# Revit family: Add_On_Board-Teknion-CQCAB_Routes-R2022
name_source: partatom
category: Furniture
units: mm (PartAtom-declared; Revit-internal decimal feet)

## family parameters
Always vertical = Yes
Cut with Voids When Loaded = No
OmniClass Number = 23.40.20.00
OmniClass Title = General Furniture and Specialties
Render Appearance Source = Family Geometry
Room Calculation Point = No
Shared = Yes
Work Plane-Based = No

## types (3) — shared parameters
2D Add On Board = Yes
Assembly Code = E2020200
Manufacturer = Teknion
Manufacturer Fax = 416.661.4586
Part Number = CQCAB
Product Documentation Link = https://assets.teknion.com
Product Line = Routes
Product Page URL = https://www.teknion.com
Series = Routes
Sustainability Data = https://www.teknion.com
URL = www.teknion.com
Unit Weight URL = http://www.teknion.com
Warranty = http://www.teknion.com
zero-valued in all types: Default Elevation

## per-type parameters (varying)
| type | Description | Left Tackboard Add On | Left Whiteboard Add On | Model | Right Tackboard Add On Board | Right Whiteboard Add On Board |
| One Whiteboard Add Ons & One Tackboard Add Ons | Routes  Add On Board, One Whiteboard Add Ons & One Tackboard Add On | No | Yes | CQCABU_ | Yes | No |
| Two Tackboard Add Ons | Routes Add On Board, Two Tackboard Add Ons | Yes | No | CQCABT_ | Yes | No |
| Two Whiteboard Add Ons | Routes Add On Board, Two Whiteboard Add Ons, | No | Yes | CQCABWW | No | Yes |

## geometry (parser evidence)
native form markers: Sweep x2
no freeform markers — native parametric forms only
